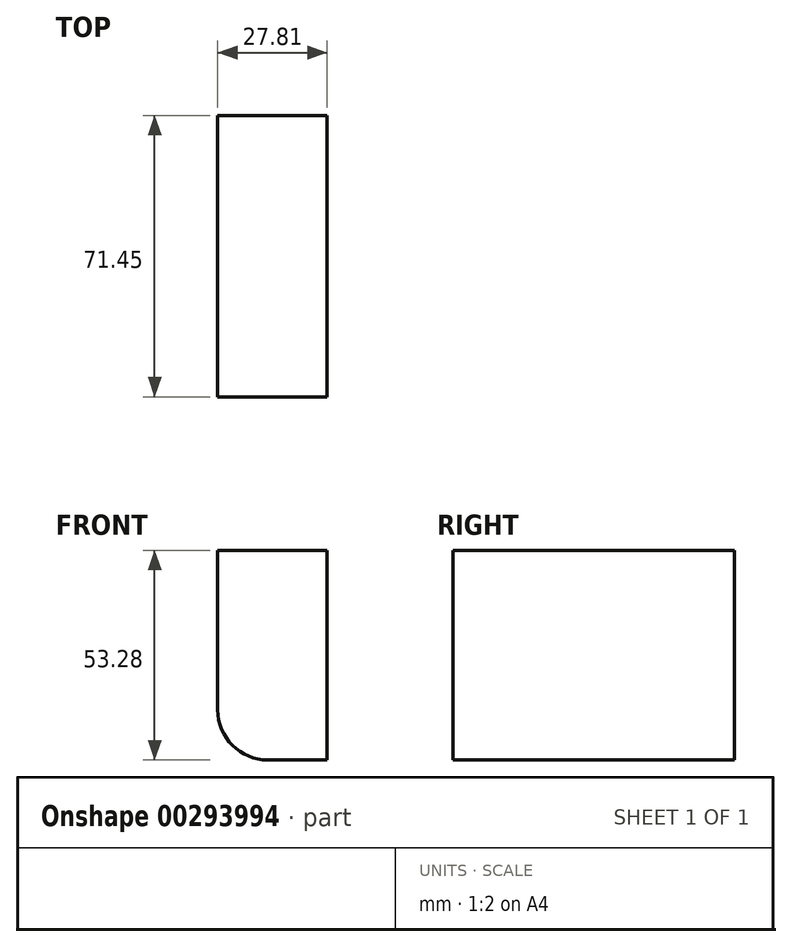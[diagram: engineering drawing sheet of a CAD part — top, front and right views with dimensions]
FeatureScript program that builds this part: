
annotation { "Feature Type Name" : "Feature", "Feature Type Description" : "" }
export const myFeature = defineFeature(function(context is Context, id is Id, definition is map)
    precondition{}
    {
        {
            var Q0;
            Q0=qCreatedBy(makeId("Front.planeOp"),FACE);
            var sketch = newSketch(context, id + "F0", { "sketchPlane" : qUnion([Q0])});
            skLineSegment(sketch, "E0.bottom", {"start": v(-42.9, -6.43) * mm, "end": v(-70.71, -6.43) * mm});
            skLineSegment(sketch, "E0.top", {"start": v(-42.9, -59.7) * mm, "end": v(-70.71, -59.7) * mm});
            skLineSegment(sketch, "E0.left", {"start": v(-42.9, -6.43) * mm, "end": v(-42.9, -59.7) * mm});
            skLineSegment(sketch, "E0.right", {"start": v(-70.71, -6.43) * mm, "end": v(-70.71, -59.7) * mm});
            skPoint(sketch, "E0.middle", {"position": v(-56.8, -33.07) * mm});
            skSolve(sketch);
        }
        {
            var Q0;
            Q0=makeQuery(id+"F0.imprint","IMPRINT",FACE,{"disambiguationData":[TD([[makeQuery(id+"F0.imprint","IMPRINT",EDGE,{"derivedFrom":sQuery(id+"F0.wireOp",EDGE,"E0.bottom")}),1.0]])]});
            extrude(context, id + "F1", {"entities" : qUnion([Q0]), "depth" : 71.45 * mm});
        }
        {
            var Q0;
            Q0=makeQuery(id+"F1.opExtrude","SWEPT_EDGE",EDGE,{"disambiguationData":[OSD([sQuery(id+"F0.wireOp",EDGE,"E0.top"),sQuery(id+"F0.wireOp",EDGE,"E0.right")])]});
            fillet(context, id + "F2", {"entities" : qUnion([Q0]), "radius" : 12.7 * mm, "tangentPropagation" : true, "allowEdgeOverflow" : false});
        }
        {
            var Q0;
            Q0=makeQuery(id+"F1.opExtrude","CAP_FACE",FACE,{"disambiguationData":[OSD([sQuery(id+"F0.wireOp",EDGE,"E0.bottom"),sQuery(id+"F0.wireOp",EDGE,"E0.top"),sQuery(id+"F0.wireOp",EDGE,"E0.left"),sQuery(id+"F0.wireOp",EDGE,"E0.right")])],"isStart":false});
            var sketch = newSketch(context, id + "F3", { "sketchPlane" : qUnion([Q0])});
            skCircle(sketch, "E1", {"center": v(-56.8, -26.72) * mm, "radius": 7.63 * mm});
            skPoint(sketch, "E1.centerSnap0", {"position": v(-70.71, -26.72) * mm});
            skPoint(sketch, "E1.centerSnap1", {"position": v(-56.8, -6.43) * mm});
            skSolve(sketch);
        }
        {
            var Q0;
            Q0=sQuery(id+"F3.wireOp",EDGE,"E1");
            extrude(context, id + "F4", {"bodyType" : ToolBodyType.SURFACE, "surfaceEntities" : qUnion([Q0]), "endBound" : BoundingType.THROUGH_ALL, "oppositeDirection" : true, "depth" : 83.06 * mm});
        }
    });
